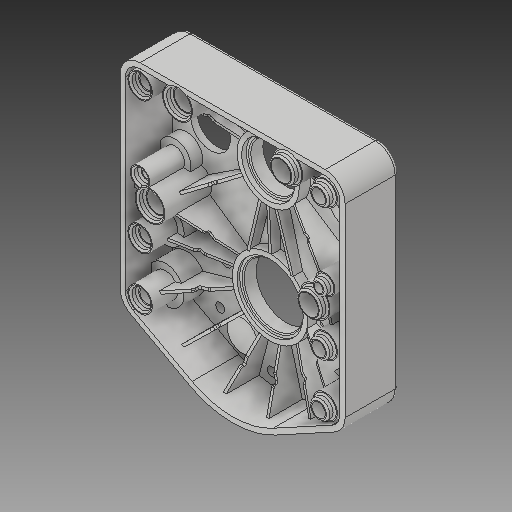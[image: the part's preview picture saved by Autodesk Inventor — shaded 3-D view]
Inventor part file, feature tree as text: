
AUTODESK INVENTOR PART (.ipt)
format: ipt  version: 2017 (Build 210142000, 142)  size: 870,912 bytes
history: native  units: in
note: dims shown in document units (in); Inventor stores cm internally (conversion verified against a paired STEP export)
features: fillet x1
ambient origin geometry x8: Origin, YZ Plane, XZ Plane, XY Plane, X Axis, Y Axis, Z Axis, Center Point
bodies: Solid1 (feature_tree)
feature tree (1):
  fillet  "Fillet18"  [1 undecoded]
note: 1 required parameter value undecoded (feature->parameter linkage not recoverable at this tier; creation-order binding heuristic only, values carry confidence <= 0.55)
